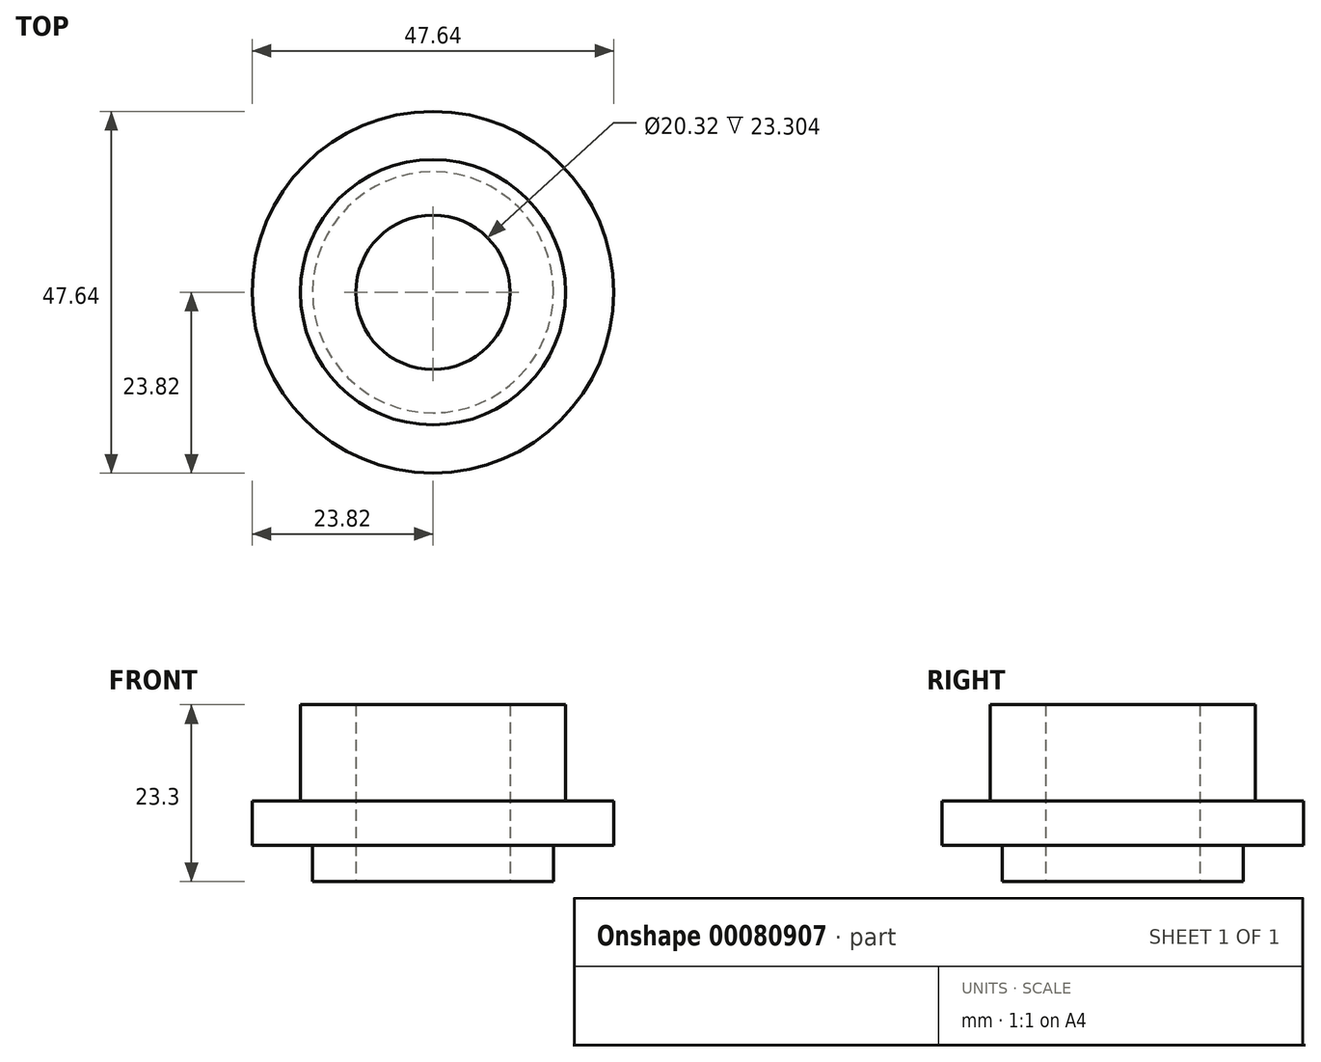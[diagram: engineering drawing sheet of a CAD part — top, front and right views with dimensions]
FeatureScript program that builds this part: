
annotation { "Feature Type Name" : "Feature", "Feature Type Description" : "" }
export const myFeature = defineFeature(function(context is Context, id is Id, definition is map)
    precondition{}
    {
        {
            var Q0;
            Q0=qCreatedBy(makeId("Front.planeOp"),FACE);
            var sketch = newSketch(context, id + "F0", { "sketchPlane" : qUnion([Q0])});
            skLineSegment(sketch, "E0", {"start": v(10.16, -10.6) * mm, "end": v(10.16, 12.7) * mm});
            skLineSegment(sketch, "E1", {"start": v(10.16, 12.7) * mm, "end": v(17.46, 12.7) * mm});
            skLineSegment(sketch, "E2", {"start": v(17.46, 12.7) * mm, "end": v(17.46, 0) * mm});
            skLineSegment(sketch, "E3", {"start": v(17.46, 0) * mm, "end": v(23.82, 0) * mm});
            skLineSegment(sketch, "E4", {"start": v(23.82, 0) * mm, "end": v(23.82, -5.84) * mm});
            skLineSegment(sketch, "E5", {"start": v(23.82, -5.84) * mm, "end": v(15.88, -5.84) * mm});
            skLineSegment(sketch, "E6", {"start": v(15.88, -5.84) * mm, "end": v(15.88, -10.6) * mm});
            skLineSegment(sketch, "E7", {"start": v(15.88, -10.6) * mm, "end": v(10.16, -10.6) * mm});
            skLineSegment(sketch, "E8", {"start": v(0, 0) * mm, "end": v(0, 19.7) * mm, "construction": true});
            skSolve(sketch);
        }
        {
            var Q0;
            Q0 = qSketchRegion(id + "F0", true);
            var Q1;
            Q1=sQuery(id+"F0.wireOp",EDGE,"E8");
            revolve(context, id + "F1", {"entities" : qUnion([Q0]), "axis" : qUnion([Q1]), "revolveType" : RevolveType.FULL});
        }
    });
